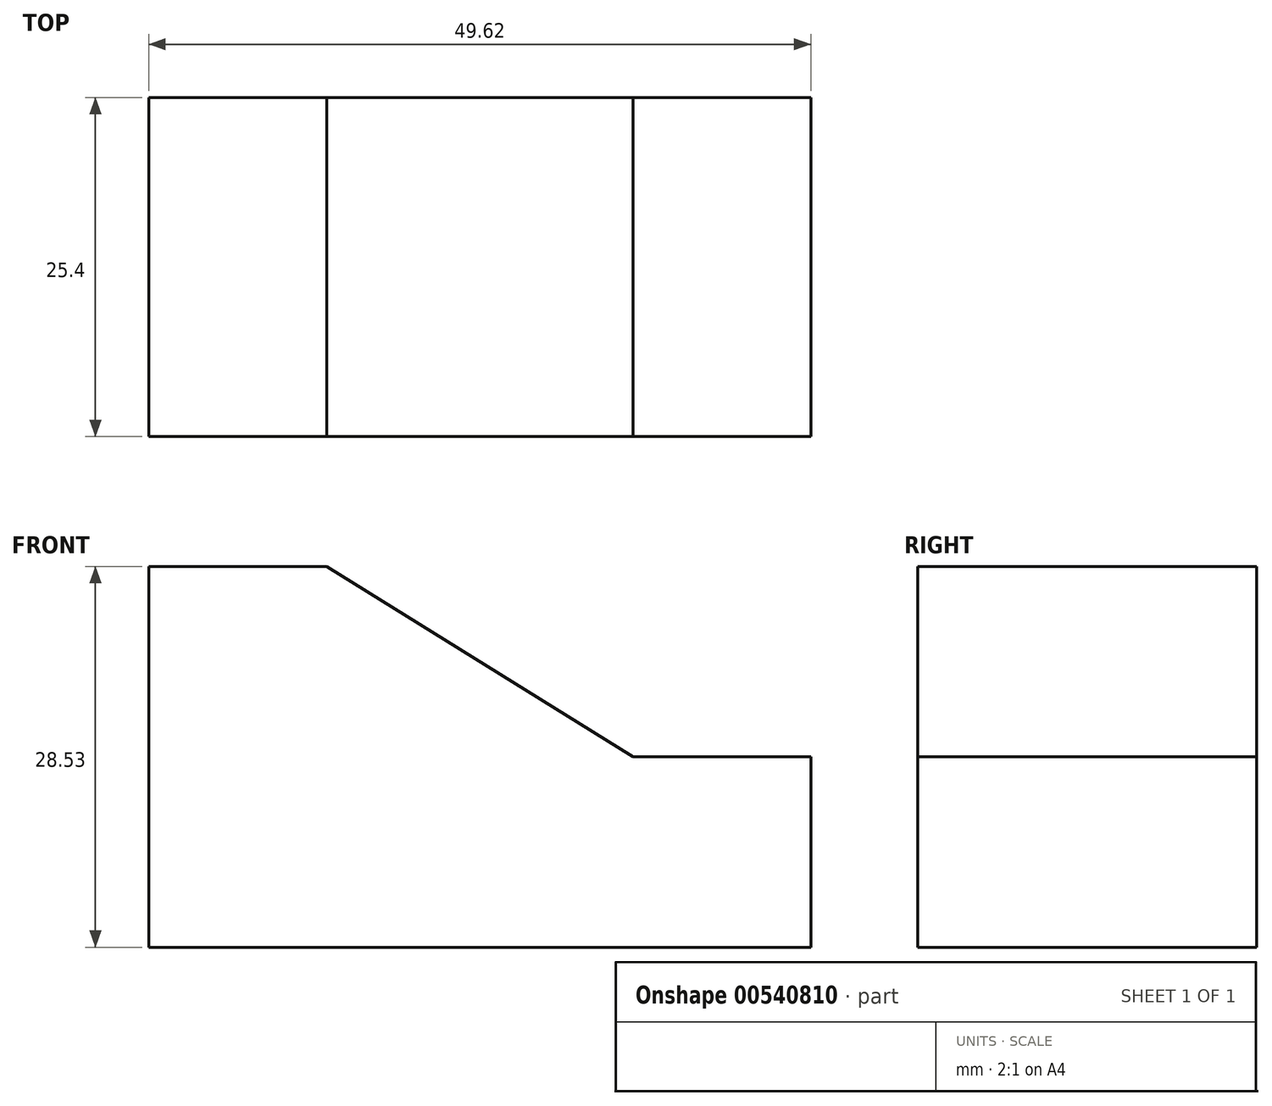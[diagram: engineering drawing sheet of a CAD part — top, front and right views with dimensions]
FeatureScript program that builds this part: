
annotation { "Feature Type Name" : "Feature", "Feature Type Description" : "" }
export const myFeature = defineFeature(function(context is Context, id is Id, definition is map)
    precondition{}
    {
        {
            var Q0;
            Q0=qCreatedBy(makeId("Front.planeOp"),FACE);
            var sketch = newSketch(context, id + "F0", { "sketchPlane" : qUnion([Q0])});
            skLineSegment(sketch, "E0", {"start": v(0, 0) * mm, "end": v(0, 28.53) * mm});
            skLineSegment(sketch, "E1", {"start": v(0, 28.53) * mm, "end": v(13.33, 28.53) * mm});
            skLineSegment(sketch, "E2", {"start": v(13.33, 28.53) * mm, "end": v(36.28, 14.27) * mm});
            skPoint(sketch, "E2.endSnap0", {"position": v(0, 14.27) * mm});
            skLineSegment(sketch, "E3", {"start": v(36.28, 14.27) * mm, "end": v(49.62, 14.27) * mm});
            skLineSegment(sketch, "E4", {"start": v(49.62, 14.27) * mm, "end": v(49.62, 0) * mm});
            skLineSegment(sketch, "E5", {"start": v(0, 0) * mm, "end": v(49.62, 0) * mm});
            skSolve(sketch);
        }
        {
            var Q0;
            Q0=makeQuery(id+"F0.imprint","IMPRINT",FACE,{"disambiguationData":[TD([[makeQuery(id+"F0.imprint","IMPRINT",EDGE,{"derivedFrom":sQuery(id+"F0.wireOp",EDGE,"E0")}),-1.0]])]});
            extrude(context, id + "F1", {"entities" : qUnion([Q0]), "depth" : 25.4 * mm, "offsetDistance" : 25.4 * mm});
        }
    });
